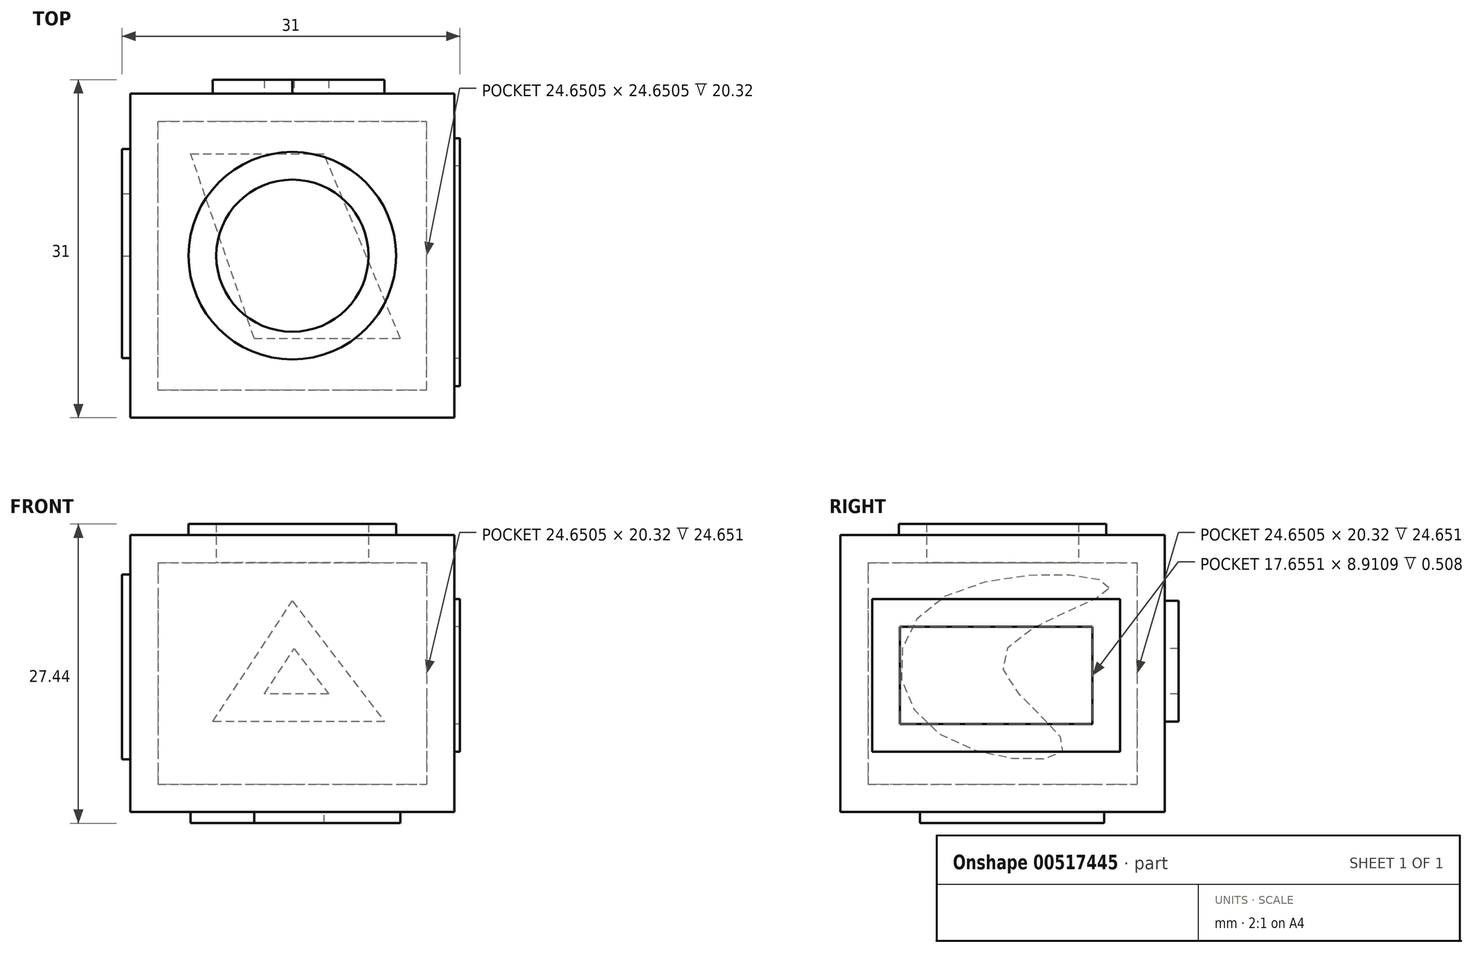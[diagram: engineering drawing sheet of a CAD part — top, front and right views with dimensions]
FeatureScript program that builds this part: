
annotation { "Feature Type Name" : "Feature", "Feature Type Description" : "" }
export const myFeature = defineFeature(function(context is Context, id is Id, definition is map)
    precondition{}
    {
        {
            var Q0;
            Q0=qCreatedBy(makeId("Top.planeOp"),FACE);
            var sketch = newSketch(context, id + "F0", { "sketchPlane" : qUnion([Q0])});
            skLineSegment(sketch, "E0.bottom", {"start": v(0.3, 0.15) * mm, "end": v(30.02, 0.15) * mm});
            skLineSegment(sketch, "E0.top", {"start": v(0.3, 29.88) * mm, "end": v(30.02, 29.88) * mm});
            skLineSegment(sketch, "E0.left", {"start": v(0.3, 0.15) * mm, "end": v(0.3, 29.88) * mm});
            skLineSegment(sketch, "E0.right", {"start": v(30.02, 0.15) * mm, "end": v(30.02, 29.88) * mm});
            skSolve(sketch);
        }
        {
            var Q0;
            Q0=makeQuery(id+"F0.imprint","IMPRINT",FACE,{"disambiguationData":[TD([[makeQuery(id+"F0.imprint","IMPRINT",EDGE,{"derivedFrom":sQuery(id+"F0.wireOp",EDGE,"E0.bottom")}),1.0]])]});
            extrude(context, id + "F1", {"entities" : qUnion([Q0]), "depth" : 25.4 * mm, "offsetDistance" : 25.4 * mm});
        }
        {
            var Q0;
            Q0=makeQuery(id+"F1.opExtrude","CAP_FACE",FACE,{"disambiguationData":[OSD([sQuery(id+"F0.wireOp",EDGE,"E0.bottom"),sQuery(id+"F0.wireOp",EDGE,"E0.top"),sQuery(id+"F0.wireOp",EDGE,"E0.left"),sQuery(id+"F0.wireOp",EDGE,"E0.right")])],"isStart":false});
            var sketch = newSketch(context, id + "F2", { "sketchPlane" : qUnion([Q0])});
            skCircle(sketch, "E1", {"center": v(15.16, 15.01) * mm, "radius": 9.52 * mm});
            skPoint(sketch, "E1.centerSnap0", {"position": v(15.16, 29.88) * mm});
            skPoint(sketch, "E1.centerSnap1", {"position": v(30.02, 15.01) * mm});
            skSolve(sketch);
        }
        {
            var Q0;
            Q0=makeQuery(id+"F2.imprint","IMPRINT",FACE,{"disambiguationData":[TD([[makeQuery(id+"F2.imprint","IMPRINT",EDGE,{"derivedFrom":sQuery(id+"F2.wireOp",EDGE,"E1")}),1.0]])]});
            extrude(context, id + "F3", {"entities" : qUnion([Q0]), "operationType" : NewBodyOperationType.ADD, "depth" : 1.02 * mm, "offsetDistance" : 25.4 * mm});
        }
        {
            var Q0;
            Q0=makeQuery(id+"F3.opExtrude","CAP_FACE",FACE,{"disambiguationData":[OSD([sQuery(id+"F2.wireOp",EDGE,"E1")])],"isStart":false});
            shell(context, id + "F4", {"entities" : qUnion([Q0]), "thickness" : 2.54 * mm});
        }
        {
            var Q0;
            Q0=makeQuery(id+"F1.opExtrude","SWEPT_FACE",FACE,{"disambiguationData":[OSD([sQuery(id+"F0.wireOp",EDGE,"E0.right")])]});
            var sketch = newSketch(context, id + "F5", { "sketchPlane" : qUnion([Q0])});
            skLineSegment(sketch, "E2.bottom", {"start": v(25.8, 19.53) * mm, "end": v(3.06, 19.53) * mm});
            skLineSegment(sketch, "E2.top", {"start": v(25.8, 5.54) * mm, "end": v(3.06, 5.54) * mm});
            skLineSegment(sketch, "E2.left", {"start": v(25.8, 19.53) * mm, "end": v(25.8, 5.54) * mm});
            skLineSegment(sketch, "E2.right", {"start": v(3.06, 19.53) * mm, "end": v(3.06, 5.54) * mm});
            skSolve(sketch);
        }
        {
            var Q0;
            Q0=makeQuery(id+"F5.imprint","IMPRINT",FACE,{"disambiguationData":[TD([[makeQuery(id+"F5.imprint","IMPRINT",EDGE,{"derivedFrom":sQuery(id+"F5.wireOp",EDGE,"E2.bottom")}),1.0]])]});
            extrude(context, id + "F6", {"entities" : qUnion([Q0]), "operationType" : NewBodyOperationType.ADD, "depth" : 0.5 * mm, "offsetDistance" : 25.4 * mm});
        }
        {
            var Q0;
            Q0=makeQuery(id+"F6.opExtrude","CAP_FACE",FACE,{"disambiguationData":[OSD([sQuery(id+"F5.wireOp",EDGE,"E2.bottom"),sQuery(id+"F5.wireOp",EDGE,"E2.top"),sQuery(id+"F5.wireOp",EDGE,"E2.left"),sQuery(id+"F5.wireOp",EDGE,"E2.right")])],"isStart":false});
            shell(context, id + "F7", {"entities" : qUnion([Q0]), "thickness" : 2.54 * mm});
        }
        {
            var Q0;
            Q0=makeQuery(id+"F1.opExtrude","SWEPT_FACE",FACE,{"disambiguationData":[OSD([sQuery(id+"F0.wireOp",EDGE,"E0.top")])]});
            var sketch = newSketch(context, id + "F8", { "sketchPlane" : qUnion([Q0])});
            skLineSegment(sketch, "E3", {"start": v(-15.16, 19.38) * mm, "end": v(-23.6, 8.3) * mm});
            skPoint(sketch, "E3.startSnap0", {"position": v(-15.16, 25.4) * mm});
            skLineSegment(sketch, "E4", {"start": v(-23.6, 8.3) * mm, "end": v(-15.16, 8.3) * mm});
            skLineSegment(sketch, "E5", {"start": v(-15.16, 8.3) * mm, "end": v(-7.87, 8.3) * mm});
            skLineSegment(sketch, "E6", {"start": v(-7.87, 8.3) * mm, "end": v(-15.16, 19.38) * mm});
            skSolve(sketch);
        }
        {
            var Q0;
            Q0=makeQuery(id+"F8.imprint","IMPRINT",FACE,{"disambiguationData":[TD([[makeQuery(id+"F8.imprint","IMPRINT",EDGE,{"derivedFrom":sQuery(id+"F8.wireOp",EDGE,"E3")}),1.0]])]});
            extrude(context, id + "F9", {"entities" : qUnion([Q0]), "operationType" : NewBodyOperationType.ADD, "depth" : 1.27 * mm, "offsetDistance" : 25.4 * mm});
        }
        {
            var Q0;
            Q0=makeQuery(id+"F9.opExtrude","CAP_FACE",FACE,{"disambiguationData":[OSD([sQuery(id+"F8.wireOp",EDGE,"E3"),sQuery(id+"F8.wireOp",EDGE,"E4"),sQuery(id+"F8.wireOp",EDGE,"E5"),sQuery(id+"F8.wireOp",EDGE,"E6")])],"isStart":false});
            shell(context, id + "F10", {"entities" : qUnion([Q0]), "thickness" : 2.54 * mm});
        }
        {
            var Q0;
            Q0=makeQuery(id+"F1.opExtrude","CAP_FACE",FACE,{"disambiguationData":[OSD([sQuery(id+"F0.wireOp",EDGE,"E0.bottom"),sQuery(id+"F0.wireOp",EDGE,"E0.top"),sQuery(id+"F0.wireOp",EDGE,"E0.left"),sQuery(id+"F0.wireOp",EDGE,"E0.right")])],"isStart":true});
            var sketch = newSketch(context, id + "F11", { "sketchPlane" : qUnion([Q0])});
            skLineSegment(sketch, "E7", {"start": v(11.66, -7.43) * mm, "end": v(25.07, -7.43) * mm});
            skLineSegment(sketch, "E8", {"start": v(25.07, -7.43) * mm, "end": v(18.07, -24.34) * mm});
            skLineSegment(sketch, "E9", {"start": v(11.66, -7.43) * mm, "end": v(5.83, -24.34) * mm});
            skLineSegment(sketch, "E10", {"start": v(5.83, -24.34) * mm, "end": v(18.07, -24.34) * mm});
            skSolve(sketch);
        }
        {
            var Q0;
            Q0=makeQuery(id+"F11.imprint","IMPRINT",FACE,{"disambiguationData":[TD([[makeQuery(id+"F11.imprint","IMPRINT",EDGE,{"derivedFrom":sQuery(id+"F11.wireOp",EDGE,"E7")}),-1.0]])]});
            extrude(context, id + "F12", {"entities" : qUnion([Q0]), "operationType" : NewBodyOperationType.ADD, "depth" : 1.02 * mm, "offsetDistance" : 25.4 * mm});
        }
        {
            var Q0;
            Q0=makeQuery(id+"F1.opExtrude","SWEPT_FACE",FACE,{"disambiguationData":[OSD([sQuery(id+"F0.wireOp",EDGE,"E0.left")])]});
            var sketch = newSketch(context, id + "F13", { "sketchPlane" : qUnion([Q0])});
            skPoint(sketch, "E11.startSnap0", {"position": v(-15.01, 25.4) * mm});
            skPoint(sketch, "E11.endSnap0", {"position": v(-29.88, 12.7) * mm});
            skPoint(sketch, "E12.endSnap0", {"position": v(-15.01, 0) * mm});
            skFitSpline(sketch, "E13", {"points": [v(-24.78, 20.55) * mm, v(-9.04, 19.38) * mm, v(-8.45, 7.72) * mm, v(-20.7, 5.98) * mm, v(-15.01, 14.14) * mm, v(-24.78, 20.55) * mm]});
            skSolve(sketch);
        }
        {
            var Q0;
            Q0=makeQuery(id+"F13.imprint","IMPRINT",FACE,{"disambiguationData":[TD([[makeQuery(id+"F13.imprint","IMPRINT",EDGE,{"derivedFrom":sQuery(id+"F13.wireOp",EDGE,"E13")}),-1.0]])]});
            extrude(context, id + "F14", {"entities" : qUnion([Q0]), "operationType" : NewBodyOperationType.ADD, "depth" : 0.76 * mm, "offsetDistance" : 25.4 * mm});
        }
    });
